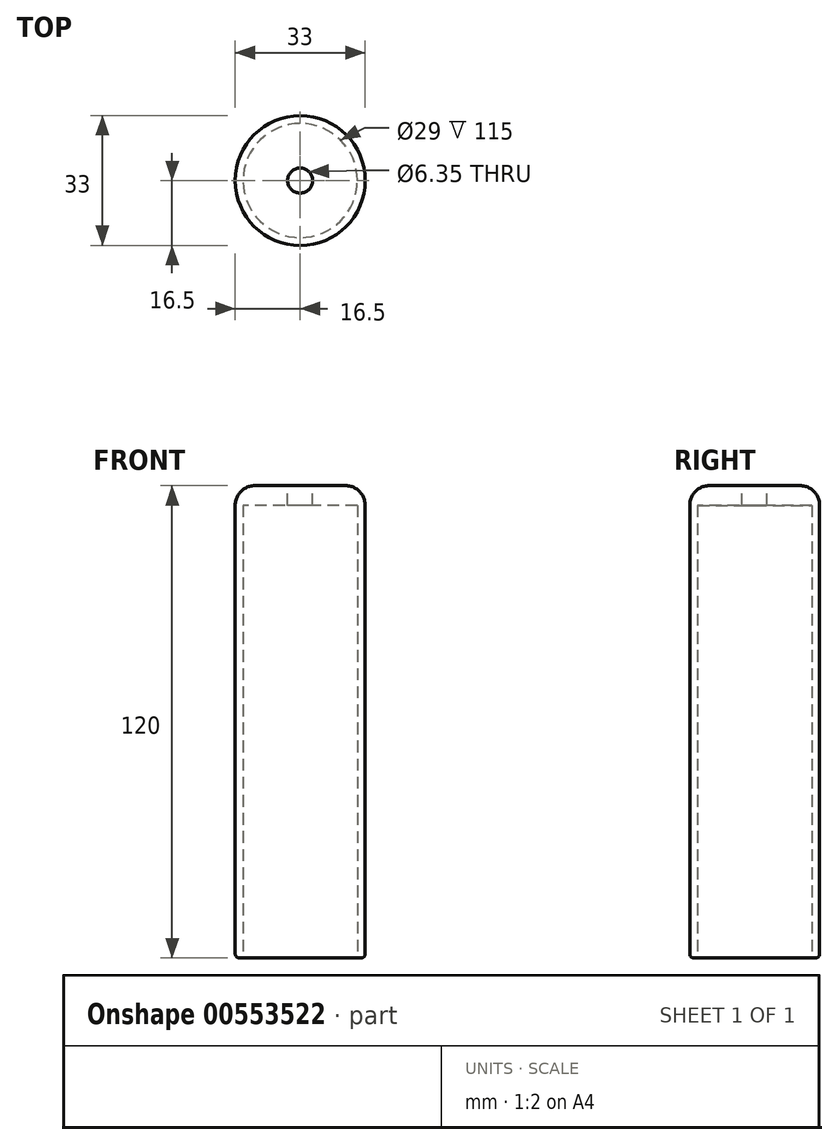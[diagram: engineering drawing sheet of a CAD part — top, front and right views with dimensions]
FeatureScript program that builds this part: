
annotation { "Feature Type Name" : "Feature", "Feature Type Description" : "" }
export const myFeature = defineFeature(function(context is Context, id is Id, definition is map)
    precondition{}
    {
        {
            var Q0;
            Q0=qCreatedBy(makeId("Top.planeOp"),FACE);
            var sketch = newSketch(context, id + "F0", { "sketchPlane" : qUnion([Q0])});
            skCircle(sketch, "E0", {"center": v(0, 0) * mm, "radius": 16.5 * mm});
            skCircle(sketch, "E1.0", {"center": v(0, 0) * mm, "radius": 14.5 * mm});
            skSolve(sketch);
        }
        {
            var Q0;
            Q0 = qSketchRegion(id + "F0", true);
            extrude(context, id + "F1", {"entities" : qUnion([Q0]), "depth" : 120 * mm, "offsetDistance" : 25 * mm});
        }
        {
            var Q0;
            Q0=makeQuery(id+"F1.opExtrude","CAP_FACE",FACE,{"disambiguationData":[OSD([sQuery(id+"F0.wireOp",EDGE,"E0"),sQuery(id+"F0.wireOp",EDGE,"E1.0")])],"isStart":false});
            var sketch = newSketch(context, id + "F2", { "sketchPlane" : qUnion([Q0])});
            skCircle(sketch, "E2.0", {"center": v(0, 0) * mm, "radius": 16.5 * mm});
            skCircle(sketch, "E3.0", {"center": v(0, 0) * mm, "radius": 14.5 * mm});
            skSolve(sketch);
        }
        {
            var Q0;
            Q0=makeQuery(id+"F2.imprint","IMPRINT",FACE,{"disambiguationData":[TD([[makeQuery(id+"F2.imprint","IMPRINT",EDGE,{"derivedFrom":sQuery(id+"F2.wireOp",EDGE,"E3.0")}),1.0]])]});
            extrude(context, id + "F3", {"entities" : qUnion([Q0]), "operationType" : NewBodyOperationType.ADD, "oppositeDirection" : true, "depth" : 5 * mm, "offsetDistance" : 25 * mm});
        }
        {
            var Q0;
            Q0=makeQuery(id+"F3.boolean.opBoolean","MERGE",FACE,{"derivedFrom":[makeQuery(id+"F1.opExtrude","CAP_FACE",FACE,{"disambiguationData":[OSD([sQuery(id+"F0.wireOp",EDGE,"E0"),sQuery(id+"F0.wireOp",EDGE,"E1.0")])],"isStart":false}),makeQuery(id+"F3.opExtrude","CAP_FACE",FACE,{"disambiguationData":[OSD([sQuery(id+"F2.wireOp",EDGE,"E3.0")])],"isStart":true})]});
            var sketch = newSketch(context, id + "F4", { "sketchPlane" : qUnion([Q0])});
            skCircle(sketch, "E4", {"center": v(0, 0) * mm, "radius": 3.18 * mm});
            skSolve(sketch);
        }
        {
            var Q0;
            Q0=makeQuery(id+"F1.opExtrude","CAP_EDGE",EDGE,{"disambiguationData":[OSD([sQuery(id+"F0.wireOp",EDGE,"E0")])],"isStart":false});
            fillet(context, id + "F5", {"entities" : qUnion([Q0]), "radius" : 5 * mm, "tangentPropagation" : true, "allowEdgeOverflow" : false});
        }
        {
            var Q0;
            Q0=makeQuery(id+"F1.opExtrude","CAP_EDGE",EDGE,{"disambiguationData":[OSD([sQuery(id+"F0.wireOp",EDGE,"E0")])],"isStart":true});
            fillet(context, id + "F6", {"entities" : qUnion([Q0]), "radius" : 1 * mm, "tangentPropagation" : true, "allowEdgeOverflow" : false});
        }
        {
            var Q0;
            Q0=makeQuery(id+"F4.imprint","IMPRINT",FACE,{"disambiguationData":[TD([[makeQuery(id+"F4.imprint","IMPRINT",EDGE,{"derivedFrom":sQuery(id+"F4.wireOp",EDGE,"E4")}),1.0]])]});
            extrude(context, id + "F7", {"entities" : qUnion([Q0]), "operationType" : NewBodyOperationType.REMOVE, "oppositeDirection" : true, "depth" : 25 * mm, "offsetDistance" : 25 * mm});
        }
    });
